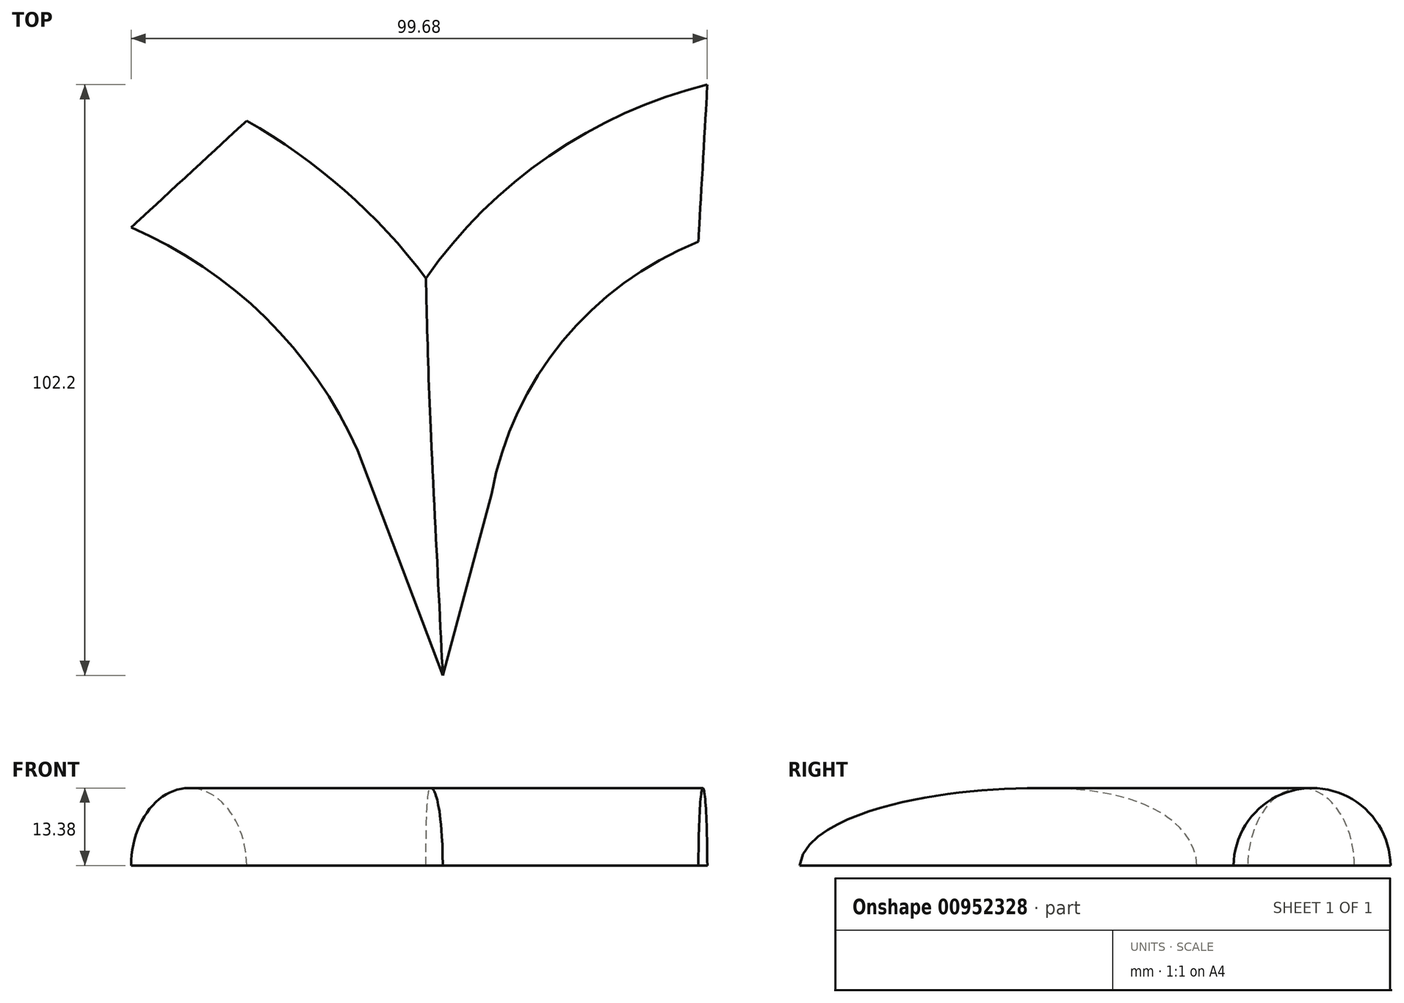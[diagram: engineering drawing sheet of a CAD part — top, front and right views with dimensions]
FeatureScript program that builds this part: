
annotation { "Feature Type Name" : "Feature", "Feature Type Description" : "" }
export const myFeature = defineFeature(function(context is Context, id is Id, definition is map)
    precondition{}
    {
        {
            var Q0;
            Q0=qCreatedBy(makeId("Top.planeOp"),FACE);
            var sketch = newSketch(context, id + "F0", { "sketchPlane" : qUnion([Q0])});
            skArc(sketch, "E0", {"start": v(0, 0) * mm, "mid": v(-16.86, 27.65) * mm, "end": v(-42.62, 47.26) * mm});
            skArc(sketch, "E1", {"start": v(46.87, 48.89) * mm, "mid": v(17.17, 30.45) * mm, "end": v(0, 0) * mm});
            skPoint(sketch, "E2.start.orphan", {"position": v(-12.47, 0) * mm});
            skSolve(sketch);
        }
        {
            var Q0;
            Q0=qCreatedBy(makeId("Front.planeOp"),FACE);
            var sketch = newSketch(context, id + "F1", { "sketchPlane" : qUnion([Q0])});
            skLineSegment(sketch, "E3", {"start": v(-12.77, 0) * mm, "end": v(14.45, 0) * mm});
            skArc(sketch, "E4", {"start": v(14.45, 0) * mm, "mid": v(0.84, 13.38) * mm, "end": v(-12.77, 0) * mm});
            skSolve(sketch);
        }
        {
            var Q0;
            Q0=makeQuery(id+"F1.imprint","IMPRINT",FACE,{"disambiguationData":[TD([[makeQuery(id+"F1.imprint","IMPRINT",EDGE,{"derivedFrom":sQuery(id+"F1.wireOp",EDGE,"E3")}),1.0]])]});
            var Q1;
            Q1=sQuery(id+"F0.wireOp",EDGE,"E1");
            var Q2;
            Q2=sQuery(id+"F0.wireOp",EDGE,"E0");
            sweep(context, id + "F2", {"profiles" : qUnion([Q0]), "path" : qUnion([Q1, Q2])});
        }
    });
